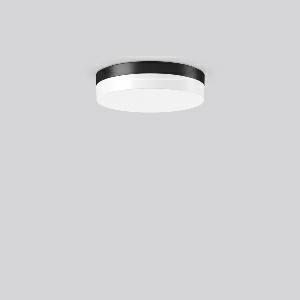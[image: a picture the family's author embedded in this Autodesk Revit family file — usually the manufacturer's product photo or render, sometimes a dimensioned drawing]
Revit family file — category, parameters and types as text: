
# Revit family: flat_slim_round_312629_0031_76_0bed
name_source: partatom
category: Lighting Fixtures
units: mm (PartAtom-declared; Revit-internal decimal feet)

## family parameters
Cut with Voids When Loaded = No
Host = Face
Light Source = No
Part Type = Normal
Room Calculation Point = No
Round Connector Dimension = Use Diameter
Shared = No

## types (1)
- MultiLumen 1 830 (1 x LED Modul 830, 1250 lm, 3000)
    Apparent Load = 13 VA
    CIE Flux Codes = 38 68 89 82 100
    Color Rendering = 80
    Color Temperature = 3000
    Default Elevation = 1800 mm
    Height = 75 mm
    Lamp = 1 x LED Modul 830
    Lamp Light Flux = 1250 lm
    Lamp count = 1
    Length = 300 mm
    Lifetime = 50000 h
    Luminous efficacy = 96 lm/W
    Manufacturer = RZB
    ModVariant = No
    Model = 312629.0031.76
    Mounting Place = Ceiling
    Mounting Type = Surface mounted
    Number of Poles = 1
    OnlyDefault = Yes
    Power Factor = 1
    Product Name = FLAT SLIM round
    Product group = Surface mounted ceiling and wall luminaires
    ProductGroupID = 305
    Protection Class = Protection class I
    Protection Degree = Degree of protection
    RLX_Detail_Level = 1
    RLX_Emergency_Light_Flux = 0 lm
    RLX_Emergency_Type = 0
    RLX_Emergency_Type_DB = No
    RlxData = <blob elided: 17629 chars, md5=774942f5>
    Socket = socket
    Standby Power = 0 W
    System Light Flux = 1250 lm
    System Power = 13 W
    Type Comments = MultiLumen 1 830
    Type Image = 312629.0031.jpg
    URL = http://relux.com
    VarID = multilumen_1_830
    Voltage = 0 V
    Weight = 0.00 kg
    Width = 0 mm  [stored 0 ft]

note: [stored X ft] marks values corroborated as IEEE doubles in the binary element streams (Revit-internal decimal feet)

## geometry (parser evidence)
native form markers: Blend x4, Sweep x13
no freeform markers — native parametric forms only
